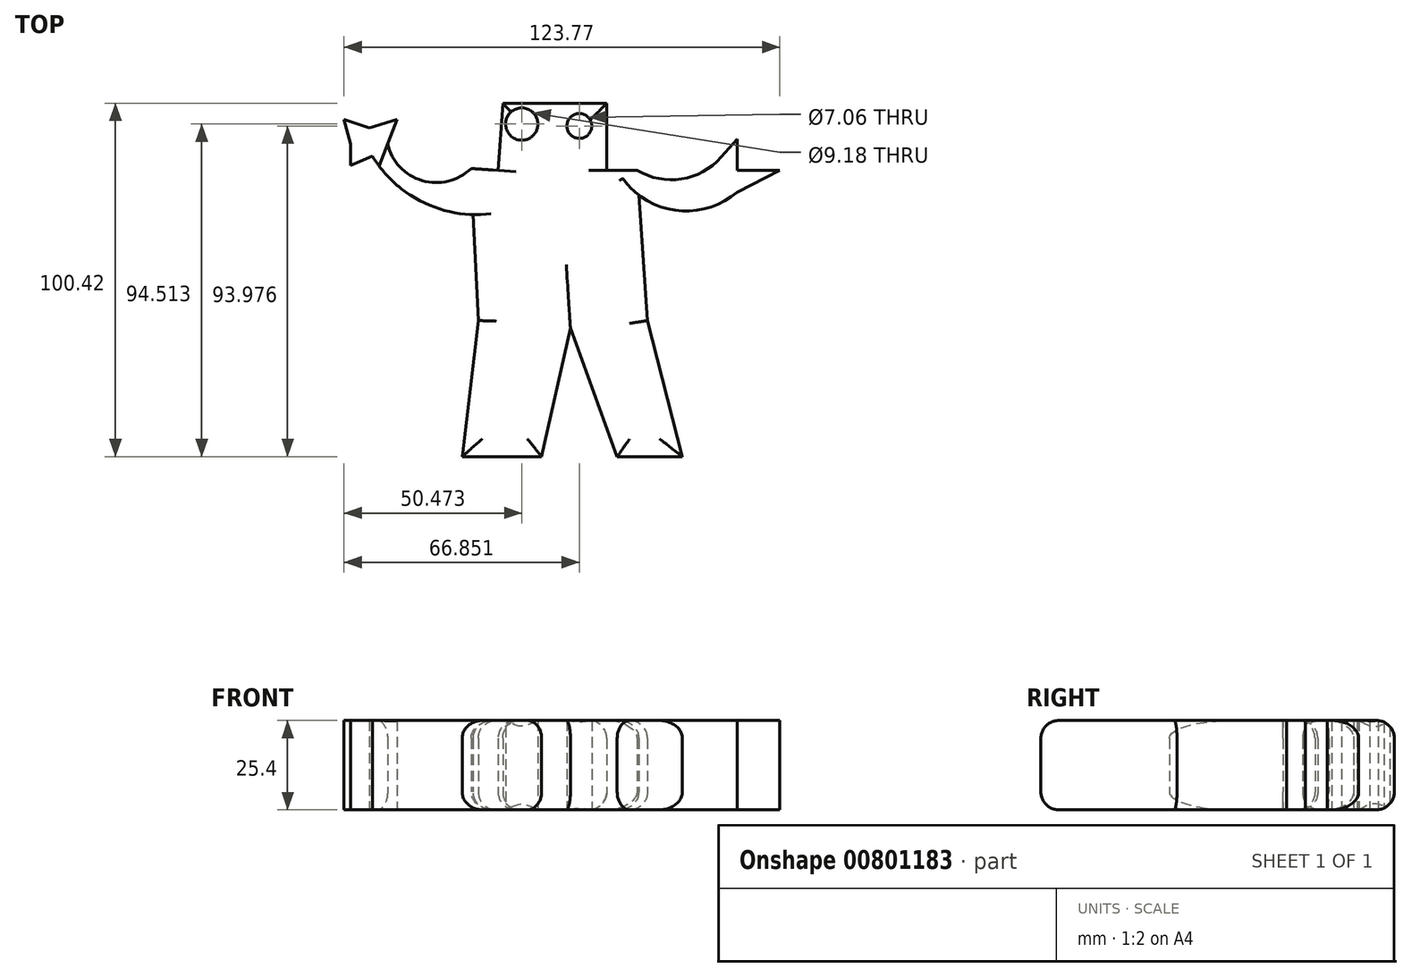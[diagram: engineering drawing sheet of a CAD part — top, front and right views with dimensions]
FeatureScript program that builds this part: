
annotation { "Feature Type Name" : "Feature", "Feature Type Description" : "" }
export const myFeature = defineFeature(function(context is Context, id is Id, definition is map)
    precondition{}
    {
        {
            var Q0;
            Q0=qCreatedBy(makeId("Top.planeOp"),FACE);
            var sketch = newSketch(context, id + "F0", { "sketchPlane" : qUnion([Q0])});
            skLineSegment(sketch, "E0", {"start": v(-20.54, 51.15) * mm, "end": v(10.34, 51.15) * mm});
            skLineSegment(sketch, "E1", {"start": v(10.34, 51.15) * mm, "end": v(10.34, 70.21) * mm});
            skLineSegment(sketch, "E2", {"start": v(10.34, 70.21) * mm, "end": v(-19.2, 70.21) * mm});
            skLineSegment(sketch, "E3", {"start": v(-19.2, 70.21) * mm, "end": v(-20.54, 51.15) * mm});
            skCircle(sketch, "E4", {"center": v(-13.83, 64.3) * mm, "radius": 4.59 * mm});
            skCircle(sketch, "E5", {"center": v(2.55, 63.77) * mm, "radius": 3.53 * mm});
            skLineSegment(sketch, "E6", {"start": v(-14.36, 55.98) * mm, "end": v(2.82, 55.98) * mm});
            skLineSegment(sketch, "E7", {"start": v(-20.54, 51.15) * mm, "end": v(-28.21, 51.69) * mm});
            skLineSegment(sketch, "E8", {"start": v(-28.21, 51.69) * mm, "end": v(-26.18, 8.46) * mm});
            skLineSegment(sketch, "E9", {"start": v(-26.18, 8.46) * mm, "end": v(21.88, 8.46) * mm});
            skLineSegment(sketch, "E10", {"start": v(21.88, 8.46) * mm, "end": v(18.93, 51.15) * mm});
            skLineSegment(sketch, "E11", {"start": v(18.93, 51.15) * mm, "end": v(10.34, 51.15) * mm});
            skLineSegment(sketch, "E12", {"start": v(-26.18, 8.46) * mm, "end": v(-30.74, -30.2) * mm});
            skLineSegment(sketch, "E13", {"start": v(-30.74, -30.2) * mm, "end": v(-8.19, -30.2) * mm});
            skLineSegment(sketch, "E14", {"start": v(-8.19, -30.2) * mm, "end": v(0, 6.3) * mm});
            skLineSegment(sketch, "E15", {"start": v(0, 6.3) * mm, "end": v(13.3, -30.2) * mm});
            skLineSegment(sketch, "E16", {"start": v(13.3, -30.2) * mm, "end": v(31.82, -30.2) * mm});
            skLineSegment(sketch, "E17", {"start": v(31.82, -30.2) * mm, "end": v(21.88, 8.46) * mm});
            skArc(sketch, "E18", {"start": v(-51.95, 58.67) * mm, "mid": v(-42.12, 48.26) * mm, "end": v(-28.21, 51.69) * mm});
            skLineSegment(sketch, "E19", {"start": v(-51.95, 58.67) * mm, "end": v(-49.27, 65.65) * mm});
            skLineSegment(sketch, "E20", {"start": v(-49.27, 65.65) * mm, "end": v(-57.05, 63.23) * mm});
            skLineSegment(sketch, "E21", {"start": v(-57.05, 63.23) * mm, "end": v(-64.3, 65.65) * mm});
            skLineSegment(sketch, "E22", {"start": v(-64.3, 65.65) * mm, "end": v(-62.42, 58.67) * mm});
            skLineSegment(sketch, "E23", {"start": v(-62.42, 58.67) * mm, "end": v(-62.42, 52.49) * mm});
            skLineSegment(sketch, "E24", {"start": v(-62.42, 52.49) * mm, "end": v(-56.25, 55.17) * mm});
            skArc(sketch, "E25", {"start": v(-56.25, 55.17) * mm, "mid": v(-44.04, 43.22) * mm, "end": v(-27.6, 38.55) * mm});
            skArc(sketch, "E26", {"start": v(18.93, 51.15) * mm, "mid": v(31.56, 48.7) * mm, "end": v(42.82, 54.9) * mm});
            skArc(sketch, "E27", {"start": v(19.41, 44.16) * mm, "mid": v(33.54, 39.58) * mm, "end": v(47.39, 44.97) * mm});
            skLineSegment(sketch, "E28", {"start": v(42.82, 54.9) * mm, "end": v(47.38, 60.08) * mm});
            skLineSegment(sketch, "E29", {"start": v(47.38, 60.08) * mm, "end": v(47.38, 51.15) * mm});
            skLineSegment(sketch, "E30", {"start": v(47.38, 51.15) * mm, "end": v(59.47, 51.15) * mm});
            skLineSegment(sketch, "E31", {"start": v(59.47, 51.15) * mm, "end": v(47.39, 44.97) * mm});
            skSolve(sketch);
        }
        {
            var Q0;
            Q0 = qSketchRegion(id + "F0", true);
            extrude(context, id + "F1", {"entities" : qUnion([Q0]), "depth" : 25.4 * mm, "offsetDistance" : 25.4 * mm});
        }
        {
            var Q0;
            Q0=makeQuery(id+"F1.opExtrude","CAP_EDGE",EDGE,{"disambiguationData":[OSD([sQuery(id+"F0.wireOp",EDGE,"E18")])],"isStart":false});
            var Q1;
            Q1=makeQuery(id+"F1.opExtrude","CAP_EDGE",EDGE,{"disambiguationData":[OSD([sQuery(id+"F0.wireOp",EDGE,"E26")])],"isStart":false});
            var Q2;
            Q2=makeQuery(id+"F1.opExtrude","CAP_EDGE",EDGE,{"disambiguationData":[OSD([sQuery(id+"F0.wireOp",EDGE,"E1")])],"isStart":false});
            var Q3;
            Q3=makeQuery(id+"F1.opExtrude","CAP_EDGE",EDGE,{"disambiguationData":[OSD([sQuery(id+"F0.wireOp",EDGE,"E2")])],"isStart":false});
            var Q4;
            Q4=makeQuery(id+"F1.opExtrude","CAP_EDGE",EDGE,{"disambiguationData":[OSD([sQuery(id+"F0.wireOp",EDGE,"E3")])],"isStart":false});
            var Q5;
            Q5=makeQuery(id+"F1.opExtrude","CAP_EDGE",EDGE,{"disambiguationData":[OSD([sQuery(id+"F0.wireOp",EDGE,"E10")])],"isStart":false});
            var Q6;
            Q6=makeQuery(id+"F1.opExtrude","CAP_EDGE",EDGE,{"disambiguationData":[OSD([sQuery(id+"F0.wireOp",EDGE,"E17")])],"isStart":false});
            var Q7;
            Q7=makeQuery(id+"F1.opExtrude","CAP_EDGE",EDGE,{"disambiguationData":[OSD([sQuery(id+"F0.wireOp",EDGE,"E15")])],"isStart":false});
            var Q8;
            Q8=makeQuery(id+"F1.opExtrude","CAP_EDGE",EDGE,{"disambiguationData":[OSD([sQuery(id+"F0.wireOp",EDGE,"E14")])],"isStart":false});
            var Q9;
            Q9=makeQuery(id+"F1.opExtrude","CAP_EDGE",EDGE,{"disambiguationData":[OSD([sQuery(id+"F0.wireOp",EDGE,"E16")])],"isStart":false});
            var Q10;
            Q10=makeQuery(id+"F1.opExtrude","CAP_EDGE",EDGE,{"disambiguationData":[OSD([sQuery(id+"F0.wireOp",EDGE,"E13")])],"isStart":false});
            var Q11;
            Q11=makeQuery(id+"F1.opExtrude","CAP_EDGE",EDGE,{"disambiguationData":[OSD([sQuery(id+"F0.wireOp",EDGE,"E12")])],"isStart":false});
            var Q12;
            Q12=makeQuery(id+"F1.opExtrude","CAP_EDGE",EDGE,{"disambiguationData":[OSD([sQuery(id+"F0.wireOp",EDGE,"E8")])],"isStart":false});
            fillet(context, id + "F2", {"entities" : qUnion([Q0, Q1, Q2, Q3, Q4, Q5, Q6, Q7, Q8, Q9, Q10, Q11, Q12]), "radius" : 5.08 * mm, "tangentPropagation" : true, "allowEdgeOverflow" : false});
        }
        {
            var Q0;
            Q0=makeQuery(id+"F1.opExtrude","CAP_EDGE",EDGE,{"disambiguationData":[OSD([sQuery(id+"F0.wireOp",EDGE,"E1")])],"isStart":true});
            var Q1;
            Q1=makeQuery(id+"F1.opExtrude","CAP_EDGE",EDGE,{"disambiguationData":[OSD([sQuery(id+"F0.wireOp",EDGE,"E3")])],"isStart":true});
            var Q2;
            Q2=makeQuery(id+"F1.opExtrude","CAP_EDGE",EDGE,{"disambiguationData":[OSD([sQuery(id+"F0.wireOp",EDGE,"E2")])],"isStart":true});
            var Q3;
            Q3=makeQuery(id+"F1.opExtrude","CAP_EDGE",EDGE,{"disambiguationData":[OSD([sQuery(id+"F0.wireOp",EDGE,"E18")])],"isStart":true});
            var Q4;
            Q4=makeQuery(id+"F1.opExtrude","CAP_EDGE",EDGE,{"disambiguationData":[OSD([sQuery(id+"F0.wireOp",EDGE,"E26")])],"isStart":true});
            var Q5;
            Q5=makeQuery(id+"F1.opExtrude","CAP_EDGE",EDGE,{"disambiguationData":[OSD([sQuery(id+"F0.wireOp",EDGE,"E10")])],"isStart":true});
            var Q6;
            Q6=makeQuery(id+"F1.opExtrude","CAP_EDGE",EDGE,{"disambiguationData":[OSD([sQuery(id+"F0.wireOp",EDGE,"E8")])],"isStart":true});
            var Q7;
            Q7=makeQuery(id+"F1.opExtrude","CAP_EDGE",EDGE,{"disambiguationData":[OSD([sQuery(id+"F0.wireOp",EDGE,"E15")])],"isStart":true});
            var Q8;
            Q8=makeQuery(id+"F1.opExtrude","CAP_EDGE",EDGE,{"disambiguationData":[OSD([sQuery(id+"F0.wireOp",EDGE,"E14")])],"isStart":true});
            var Q9;
            Q9=makeQuery(id+"F1.opExtrude","CAP_EDGE",EDGE,{"disambiguationData":[OSD([sQuery(id+"F0.wireOp",EDGE,"E12")])],"isStart":true});
            var Q10;
            Q10=makeQuery(id+"F1.opExtrude","CAP_EDGE",EDGE,{"disambiguationData":[OSD([sQuery(id+"F0.wireOp",EDGE,"E17")])],"isStart":true});
            var Q11;
            Q11=makeQuery(id+"F1.opExtrude","CAP_EDGE",EDGE,{"disambiguationData":[OSD([sQuery(id+"F0.wireOp",EDGE,"E16")])],"isStart":true});
            var Q12;
            Q12=makeQuery(id+"F1.opExtrude","CAP_EDGE",EDGE,{"disambiguationData":[OSD([sQuery(id+"F0.wireOp",EDGE,"E13")])],"isStart":true});
            fillet(context, id + "F3", {"entities" : qUnion([Q0, Q1, Q2, Q3, Q4, Q5, Q6, Q7, Q8, Q9, Q10, Q11, Q12]), "radius" : 5.08 * mm, "tangentPropagation" : true, "allowEdgeOverflow" : false});
        }
    });
